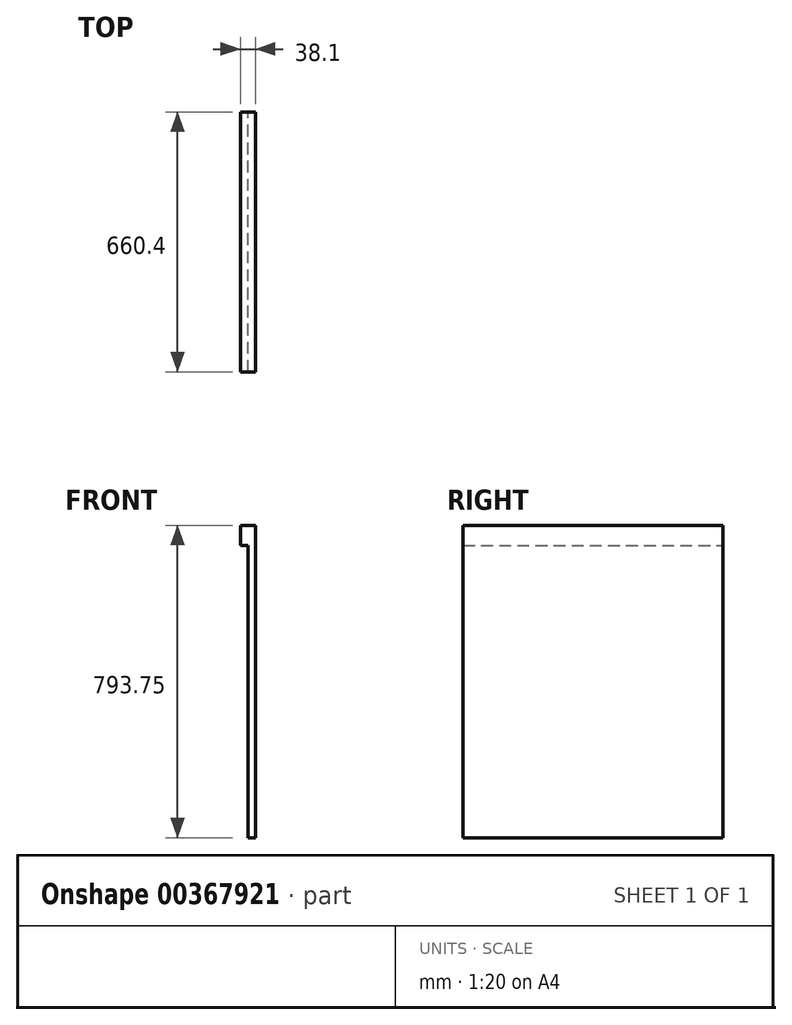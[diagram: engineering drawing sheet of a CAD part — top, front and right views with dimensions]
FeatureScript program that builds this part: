
annotation { "Feature Type Name" : "Feature", "Feature Type Description" : "" }
export const myFeature = defineFeature(function(context is Context, id is Id, definition is map)
    precondition{}
    {
        {
            var Q0;
            Q0=qCreatedBy(makeId("Right.planeOp"),FACE);
            var sketch = newSketch(context, id + "F0", { "sketchPlane" : qUnion([Q0])});
            skLineSegment(sketch, "E0.bottom", {"start": v(-305.68, 379.3) * mm, "end": v(354.72, 379.3) * mm});
            skLineSegment(sketch, "E0.top", {"start": v(-305.68, -414.45) * mm, "end": v(354.72, -414.45) * mm});
            skLineSegment(sketch, "E0.left", {"start": v(-305.68, 379.3) * mm, "end": v(-305.68, -414.45) * mm});
            skLineSegment(sketch, "E0.right", {"start": v(354.72, 379.3) * mm, "end": v(354.72, -414.45) * mm});
            skLineSegment(sketch, "E1.top", {"start": v(-305.68, 328.5) * mm, "end": v(354.72, 328.5) * mm});
            skLineSegment(sketch, "E1.left", {"start": v(-305.68, 379.3) * mm, "end": v(-305.68, 328.5) * mm});
            skLineSegment(sketch, "E1.right", {"start": v(354.72, 379.3) * mm, "end": v(354.72, 328.5) * mm});
            skSolve(sketch);
        }
        {
            var Q0;
            Q0=makeQuery(id+"F0.imprint","IMPRINT",FACE,{"disambiguationData":[TD([[makeQuery(id+"F0.imprint","IMPRINT",EDGE,{"derivedFrom":sQuery(id+"F0.wireOp",EDGE,"E0.bottom")}),-1.0]])]});
            extrude(context, id + "F1", {"entities" : qUnion([Q0]), "depth" : 19.05 * mm});
        }
        {
            var Q0;
            Q0=makeQuery(id+"F0.imprint","IMPRINT",FACE,{"disambiguationData":[TD([[makeQuery(id+"F0.imprint","IMPRINT",EDGE,{"derivedFrom":sQuery(id+"F0.wireOp",EDGE,"E0.bottom")}),-1.0]])]});
            extrude(context, id + "F2", {"entities" : qUnion([Q0]), "oppositeDirection" : true, "depth" : 19.05 * mm});
        }
        {
            var Q0;
            Q0=makeQuery(id+"F0.imprint","IMPRINT",FACE,{"disambiguationData":[TD([[makeQuery(id+"F0.imprint","IMPRINT",EDGE,{"derivedFrom":sQuery(id+"F0.wireOp",EDGE,"E0.bottom")}),-1.0]])]});
            var Q1;
            Q1=makeQuery(id+"F0.imprint","IMPRINT",FACE,{"disambiguationData":[TD([[makeQuery(id+"F0.imprint","IMPRINT",EDGE,{"derivedFrom":sQuery(id+"F0.wireOp",EDGE,"E0.top")}),1.0]])]});
            extrude(context, id + "F3", {"entities" : qUnion([Q0, Q1]), "operationType" : NewBodyOperationType.ADD, "depth" : 19.05 * mm});
        }
    });
